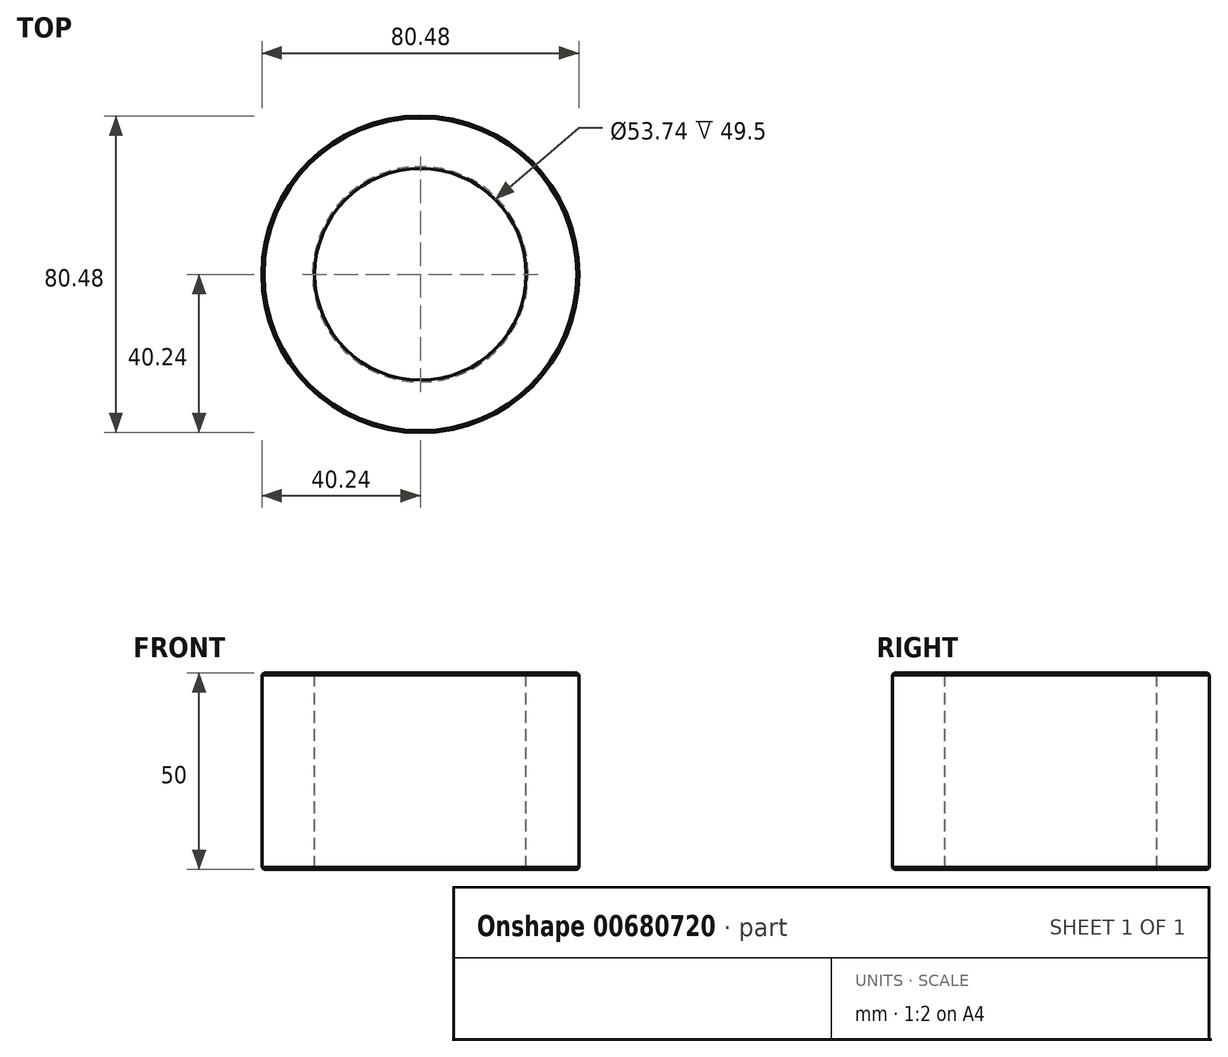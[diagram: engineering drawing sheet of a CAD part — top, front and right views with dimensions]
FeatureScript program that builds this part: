
annotation { "Feature Type Name" : "Feature", "Feature Type Description" : "" }
export const myFeature = defineFeature(function(context is Context, id is Id, definition is map)
    precondition{}
    {
        {
            var Q0;
            Q0=qCreatedBy(makeId("Top.planeOp"),FACE);
            var sketch = newSketch(context, id + "F0", { "sketchPlane" : qUnion([Q0])});
            skCircle(sketch, "E0", {"center": v(0, 0) * mm, "radius": 40.24 * mm});
            skSolve(sketch);
        }
        {
            var Q0;
            Q0=makeQuery(id+"F0.imprint","IMPRINT",FACE,{"disambiguationData":[TD([[makeQuery(id+"F0.imprint","IMPRINT",EDGE,{"derivedFrom":sQuery(id+"F0.wireOp",EDGE,"E0")}),1.0]])]});
            var Q1;
            Q1 = qSketchRegion(id + "F0", true);
            extrude(context, id + "F1", {"entities" : qUnion([Q0, Q1]), "depth" : 50 * mm, "offsetDistance" : 25.4 * mm});
        }
        {
            var Q0;
            Q0=makeQuery(id+"F1.opExtrude","CAP_FACE",FACE,{"disambiguationData":[OSD([sQuery(id+"F0.wireOp",EDGE,"E0")])],"isStart":false});
            var sketch = newSketch(context, id + "F2", { "sketchPlane" : qUnion([Q0])});
            skCircle(sketch, "E1", {"center": v(0, 0) * mm, "radius": 26.87 * mm});
            skSolve(sketch);
        }
        {
            var Q0;
            Q0=makeQuery(id+"F2.imprint","IMPRINT",FACE,{"disambiguationData":[TD([[makeQuery(id+"F2.imprint","IMPRINT",EDGE,{"derivedFrom":sQuery(id+"F2.wireOp",EDGE,"E1")}),1.0]])]});
            extrude(context, id + "F3", {"entities" : qUnion([Q0]), "operationType" : NewBodyOperationType.REMOVE, "oppositeDirection" : true, "depth" : 62 * mm, "offsetDistance" : 25.4 * mm});
        }
        {
            var Q0;
            Q0=makeQuery(id+"F1.opExtrude","CAP_EDGE",EDGE,{"disambiguationData":[OSD([sQuery(id+"F0.wireOp",EDGE,"E0")])],"isStart":false});
            var Q1;
            Q1=makeQuery(id+"F3.boolean.opBoolean","COPY",EDGE,{"derivedFrom":makeQuery(id+"F3.opExtrude","CAP_EDGE",EDGE,{"disambiguationData":[OSD([sQuery(id+"F2.wireOp",EDGE,"E1")])],"isStart":true})});
            var Q2;
            Q2=makeQuery(id+"F1.opExtrude","CAP_EDGE",EDGE,{"disambiguationData":[OSD([sQuery(id+"F0.wireOp",EDGE,"E0")])],"isStart":true});
            var Q3;
            Q3=makeQuery(id+"F3.boolean.opBoolean","INTERSECT",EDGE,{"derivedFrom":[makeQuery(id+"F1.opExtrude","CAP_FACE",FACE,{"disambiguationData":[OSD([sQuery(id+"F0.wireOp",EDGE,"E0")])],"isStart":true}),makeQuery(id+"F3.opExtrude","SWEPT_FACE",FACE,{"disambiguationData":[OSD([sQuery(id+"F2.wireOp",EDGE,"E1")])]})]});
            chamfer(context, id + "F4", {"entities" : qUnion([Q0, Q1, Q2, Q3]), "width" : 0.5 * mm, "tangentPropagation" : true});
        }
    });
